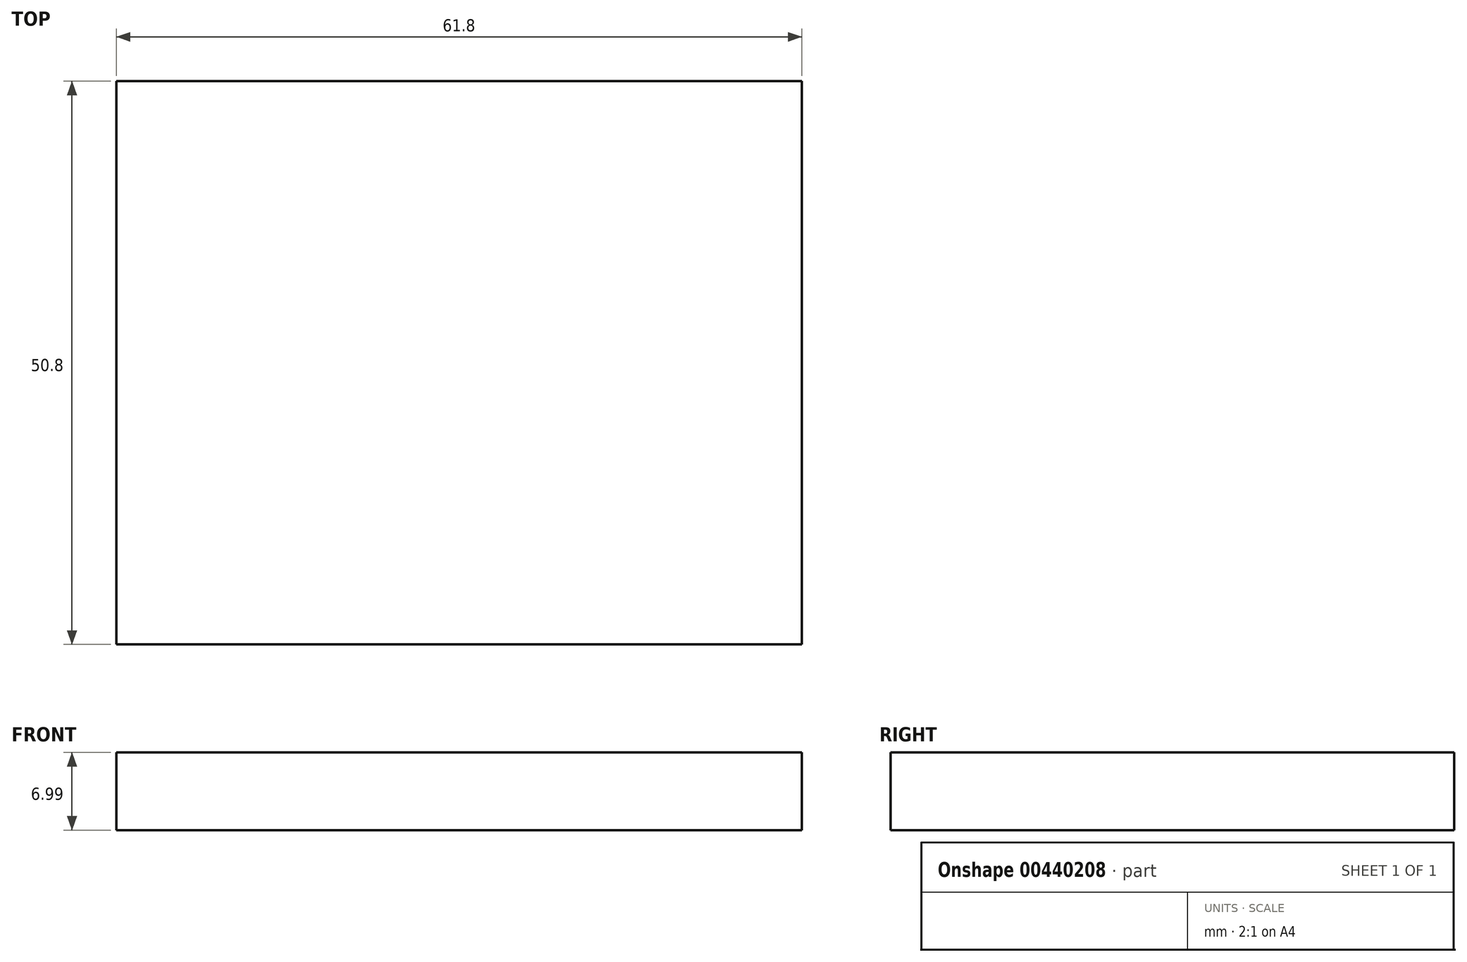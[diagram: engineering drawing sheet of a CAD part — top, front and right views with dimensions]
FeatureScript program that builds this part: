
annotation { "Feature Type Name" : "Feature", "Feature Type Description" : "" }
export const myFeature = defineFeature(function(context is Context, id is Id, definition is map)
    precondition{}
    {
        {
            var Q0;
            Q0=qCreatedBy(makeId("Front.planeOp"),FACE);
            var sketch = newSketch(context, id + "F0", { "sketchPlane" : qUnion([Q0])});
            skLineSegment(sketch, "E0", {"start": v(-63.97, 19.28) * mm, "end": v(-63.97, 12.3) * mm});
            skLineSegment(sketch, "E1", {"start": v(-63.97, 12.3) * mm, "end": v(-2.17, 12.3) * mm});
            skLineSegment(sketch, "E2", {"start": v(-2.17, 12.3) * mm, "end": v(-2.17, 19.28) * mm});
            skLineSegment(sketch, "E3", {"start": v(-2.17, 19.28) * mm, "end": v(-63.97, 19.28) * mm});
            skSolve(sketch);
        }
        {
            var Q0;
            Q0 = qSketchRegion(id + "F0", true);
            extrude(context, id + "F1", {"entities" : qUnion([Q0]), "depth" : 50.8 * mm});
        }
    });
